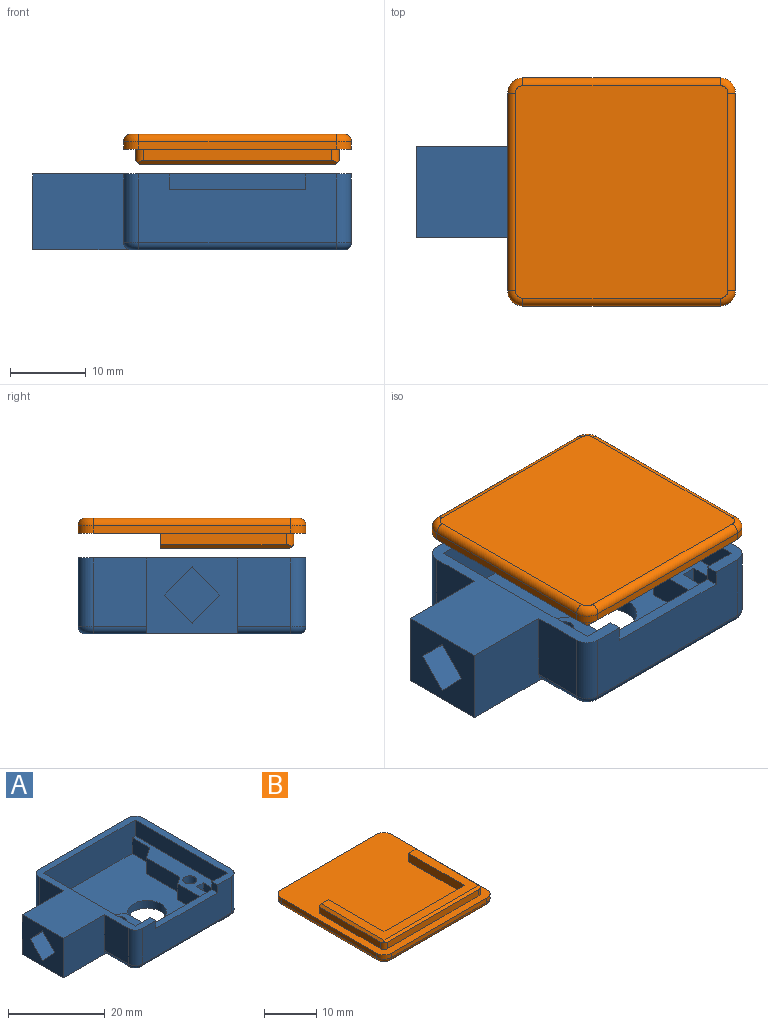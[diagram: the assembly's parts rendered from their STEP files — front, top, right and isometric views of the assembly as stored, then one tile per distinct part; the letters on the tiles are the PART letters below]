
ASSEMBLY  parts=2 mates=2
PART A: 63 faces, bbox 42.2x30.3x10 mm
  f0: plane 26.8x4mm, normal (0,1,0), area 71.3mm2, adj f2,f4,f5,f35,f60,f61,f62
  f1: plane 26x9mm, normal (0,-1,0), area 198.1mm2, adj f2,f47,f48,f53,f60,f61,f62
  f2: plane 42x30mm, normal (0,0,1), area 293.5mm2, adj f0,f1,f4,f5,f6,f7,f8,f9
  f3: plane 5.13x4mm, normal (-1,0,0), area 20.5mm2, adj f13,f25,f35,f37
  f4: plane 26.8x4mm, normal (-1,0,0), area 107.2mm2, adj f0,f2,f13,f35
  f5: plane 26.8x4mm, normal (1,0,0), area 107.2mm2, adj f0,f2,f13,f35
  f6: plane 9x7mm, normal (-1,0,0), area 63mm2, adj f2,f7,f50,f59
  f7: plane 13x10mm, normal (0,1,0), area 120.2mm2, adj f2,f6,f8,f14,f59
  f8: plane 12x10mm, normal (-1,0,0), area 93mm2, adj f2,f7,f9,f14,f42,f43,f44,f45
  f9: plane 13x10mm, normal (0,-1,0), area 120.2mm2, adj f2,f8,f10,f14,f51
  f10: plane 9x7mm, normal (-1,0,0), area 63mm2, adj f2,f9,f47,f51
  f11: plane 26x9mm, normal (1,0,0), area 234mm2, adj f2,f48,f49,f55
  f12: plane 26x9mm, normal (0,1,0), area 234mm2, adj f2,f49,f50,f57
  f13: plane 26.8x8mm, normal (0,-1,0), area 207.2mm2, adj f2,f3,f4,f5,f24,f35,f37
  f14: plane 41x28mm, normal (0,0,-1), area 888.9mm2, adj f7,f8,f9,f36,f51,f52,f53,f54
  f15: plane 4x2mm, normal (0,-1,0), area 8mm2, adj f16,f34,f35,f39
  f16: plane 4x3.12mm, normal (-1,0,0), area 12.5mm2, adj f15,f17,f35,f39
  f17: plane 4x2mm, normal (0,1,0), area 8mm2, adj f16,f34,f35,f39
  f18: plane 4x2mm, normal (0,1,0), area 8mm2, adj f19,f32,f35,f40
  f19: plane 4x3.12mm, normal (1,0,0), area 12.5mm2, adj f18,f20,f35,f40
  f20: plane 4x2mm, normal (0,-1,0), area 8mm2, adj f19,f32,f35,f40
  f21: plane 4x2mm, normal (0.57,0.82,0), area 9.8mm2, adj f22,f33,f35,f37
  f22: plane 9.67x4mm, normal (1,0,0), area 38.7mm2, adj f21,f23,f35,f37
  f23: plane 4x3mm, normal (0.57,0.82,0), area 14.6mm2, adj f22,f24,f35,f37
  f24: plane 5.13x4mm, normal (1,0,0), area 20.5mm2, adj f13,f23,f35,f37
  f25: plane 4x3mm, normal (-0.57,0.82,0), area 14.6mm2, adj f3,f26,f35,f37
  f26: plane 9.67x4mm, normal (-1,0,0), area 38.7mm2, adj f25,f27,f35,f37
  f27: plane 4x2mm, normal (-0.57,0.82,0), area 9.8mm2, adj f26,f28,f35,f37
  f28: plane 7.6x4mm, normal (-1,0,0), area 30.4mm2, adj f27,f29,f35,f37
  f29: plane 15x4mm, normal (0,1,0), area 60mm2, adj f28,f33,f35,f37
  f30: cylinder r=1.45mm len=4mm, axis (0,0,-1), area 36.3mm2, adj f35,f38
  f31: cylinder r=1.45mm len=4mm, axis (0,0,-1), area 36.3mm2, adj f35,f41
  f32: plane 4x3.12mm, normal (-1,0,0), area 12.5mm2, adj f18,f20,f35,f40
  f33: plane 7.6x4mm, normal (1,0,0), area 30.4mm2, adj f21,f29,f35,f37
  f34: plane 4x3.12mm, normal (1,0,0), area 12.5mm2, adj f15,f17,f35,f39
  f35: plane 26.8x26.8mm, normal (0,0,1), area 196.6mm2, adj f0,f3,f4,f5,f13,f15,f16,f17
  f36: cylinder r=4mm len=8mm, axis (0,0,-1), area 50.3mm2, adj f14,f37
  f37: plane 25.9x25mm, normal (0,0,1), area 445.7mm2, adj f3,f13,f21,f22,f23,f24,f25,f26
  f38: plane 2.89x2.89mm, normal (0,0,1), area 6.6mm2, adj f30
  f39: plane 3.12x2mm, normal (0,0,1), area 6.2mm2, adj f15,f16,f17,f34
  f40: plane 3.12x2mm, normal (0,0,1), area 6.2mm2, adj f18,f19,f20,f32
  f41: plane 2.89x2.89mm, normal (0,0,1), area 6.6mm2, adj f31
  f42: plane 12x3.75mm, normal (0,-0.72,-0.69), area 62.4mm2, adj f8,f43,f45,f46
  f43: plane 12x3.75mm, normal (0,-0.72,0.69), area 62.4mm2, adj f8,f42,f44,f46
  f44: plane 12x3.75mm, normal (0,0.72,0.69), area 62.4mm2, adj f8,f43,f45,f46
  f45: plane 12x3.75mm, normal (0,0.72,-0.69), area 62.4mm2, adj f8,f42,f44,f46
  f46: plane 7.5x7.2mm, normal (-1,0,0), area 27mm2, adj f42,f43,f44,f45
  f47: cylinder r=2mm len=9mm, axis (0,0,1), area 28.3mm2, adj f1,f2,f10,f52
  f48: cylinder r=2mm len=9mm, axis (0,0,-1), area 28.3mm2, adj f1,f2,f11,f54
  f49: cylinder r=2mm len=9mm, axis (0,0,1), area 28.3mm2, adj f2,f11,f12,f56
  f50: cylinder r=2mm len=9mm, axis (0,0,-1), area 28.3mm2, adj f2,f6,f12,f58
  f51: cylinder r=1mm len=7mm, axis (0,-1,0), area 11mm2, adj f9,f10,f14,f52
  f52: torus R=1mm, axis (0,0,1), area 4mm2, adj f14,f47,f51,f53
  f53: cylinder r=1mm len=26mm, axis (1,0,0), area 40.8mm2, adj f1,f14,f52,f54
  f54: torus R=1mm, axis (0,0,1), area 4mm2, adj f14,f48,f53,f55
  f55: cylinder r=1mm len=26mm, axis (0,1,0), area 40.8mm2, adj f11,f14,f54,f56
  f56: torus R=1mm, axis (0,0,1), area 4mm2, adj f14,f49,f55,f57
  f57: cylinder r=1mm len=26mm, axis (-1,0,0), area 40.8mm2, adj f12,f14,f56,f58
  f58: torus R=1mm, axis (0,0,1), area 4mm2, adj f14,f50,f57,f59
  f59: cylinder r=1mm len=7mm, axis (0,-1,0), area 11mm2, adj f6,f7,f14,f58
  f60: plane 18x1.6mm, normal (0,0,1), area 28.8mm2, adj f0,f1,f61,f62
  f61: plane 1.99x1.6mm, normal (-1,0,0), area 3.2mm2, adj f0,f1,f2,f60
  f62: plane 1.99x1.6mm, normal (1,0,0), area 3.2mm2, adj f0,f1,f2,f60
PART B: 32 faces, bbox 30.3x30.3x4 mm
  f0: plane 26x1mm, normal (0,-1,0), area 26mm2, adj f4,f15,f18,f29
  f1: plane 26x1mm, normal (1,0,0), area 26mm2, adj f4,f15,f16,f25
  f2: plane 26x1mm, normal (0,1,0), area 26mm2, adj f4,f16,f17,f22
  f3: plane 26x1mm, normal (-1,0,0), area 26mm2, adj f4,f17,f18,f26
  f4: plane 30x30mm, normal (0,0,1), area 754.6mm2, adj f0,f1,f2,f3,f6,f7,f8,f9
  f5: plane 28x28mm, normal (0,0,-1), area 783.1mm2, adj f22,f23,f24,f25,f26,f27,f28,f29
  f6: plane 16.58x1.5mm, normal (1,0,0), area 24.9mm2, adj f4,f7,f19,f30
  f7: plane 2.5x2mm, normal (0,1,0), area 4.9mm2, adj f4,f6,f8,f14,f19
  f8: plane 15.08x2mm, normal (-1,0,0), area 30.2mm2, adj f4,f7,f9,f14
  f9: plane 21.8x2mm, normal (0,1,0), area 43.6mm2, adj f4,f8,f10,f14
  f10: plane 15.08x2mm, normal (1,0,0), area 30.2mm2, adj f4,f9,f11,f14
  f11: plane 2.5x2mm, normal (0,1,0), area 4.9mm2, adj f4,f10,f12,f14,f21
  f12: plane 16.58x1.5mm, normal (-1,0,0), area 24.9mm2, adj f4,f11,f21,f31
  f13: plane 24.8x1.5mm, normal (0,-1,0), area 37.2mm2, adj f4,f20,f30,f31
  f14: plane 25.8x17.08mm, normal (0,0,1), area 111.9mm2, adj f7,f8,f9,f10,f11,f19,f20,f21
  f15: cylinder r=2mm len=2mm, axis (0,0,-1), area 3.1mm2, adj f0,f1,f4,f27
  f16: cylinder r=2mm len=2mm, axis (0,0,1), area 3.1mm2, adj f1,f2,f4,f23
  f17: cylinder r=2mm len=2mm, axis (0,0,-1), area 3.1mm2, adj f2,f3,f4,f24
  f18: cylinder r=2mm len=2mm, axis (0,0,1), area 3.1mm2, adj f0,f3,f4,f28
  f19: plane 17.28x0.5mm, normal (0.71,0,0.71), area 12.1mm2, adj f6,f7,f14,f20,f30
  f20: plane 26.21x0.5mm, normal (0,-0.71,0.71), area 18.3mm2, adj f13,f14,f19,f21,f30,f31
  f21: plane 17.28x0.5mm, normal (-0.71,0,0.71), area 12.1mm2, adj f11,f12,f14,f20,f31
  f22: cylinder r=1mm len=26mm, axis (-1,0,0), area 40.8mm2, adj f2,f5,f23,f24
  f23: torus R=1mm, axis (0,0,1), area 4mm2, adj f5,f16,f22,f25
  f24: torus R=1mm, axis (0,0,1), area 4mm2, adj f5,f17,f22,f26
  f25: cylinder r=1mm len=26mm, axis (0,1,0), area 40.8mm2, adj f1,f5,f23,f27
  f26: cylinder r=1mm len=26mm, axis (0,-1,0), area 40.8mm2, adj f3,f5,f24,f28
  f27: torus R=1mm, axis (0,0,1), area 4mm2, adj f5,f15,f25,f29
  f28: torus R=1mm, axis (0,0,1), area 4mm2, adj f5,f18,f26,f29
  f29: cylinder r=1mm len=26mm, axis (1,0,0), area 40.8mm2, adj f0,f5,f27,f28
  f30: cylinder r=1mm len=1.79mm, axis (0,0,-1), area 2.5mm2, adj f4,f6,f13,f19,f20
  f31: cylinder r=1mm len=1.79mm, axis (0,0,1), area 2.5mm2, adj f4,f12,f13,f20,f21
PLACE A t=(-4.1,-10.13,-11.43)mm fixed
PLACE B rot(axis=(0,1,0),180deg) t=(-4.1,-10.13,3.83)mm
MATE planar B.f13 <-> A.f0  axis (0,-1,0) through (-4.1,-23.53,1.08)mm
MATE planar B.f6 <-> A.f5  axis (-1,0,0) through (-17.5,-14.25,1.08)mm
